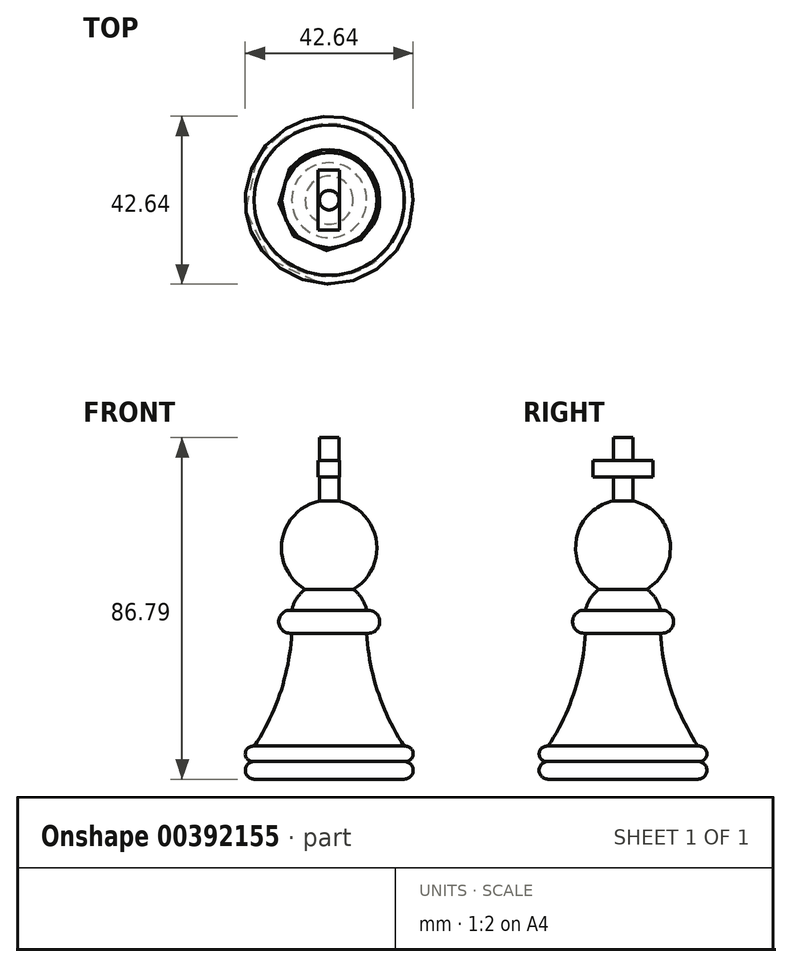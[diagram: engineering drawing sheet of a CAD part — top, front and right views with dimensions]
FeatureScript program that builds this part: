
annotation { "Feature Type Name" : "Feature", "Feature Type Description" : "" }
export const myFeature = defineFeature(function(context is Context, id is Id, definition is map)
    precondition{}
    {
        {
            var Q0;
            Q0=qCreatedBy(makeId("Front.planeOp"),FACE);
            var sketch = newSketch(context, id + "F0", { "sketchPlane" : qUnion([Q0])});
            skLineSegment(sketch, "E0", {"start": v(0, 33.3) * mm, "end": v(0, -42.9) * mm});
            skLineSegment(sketch, "E1", {"start": v(0, -42.9) * mm, "end": v(-19.05, -42.9) * mm});
            skArc(sketch, "E2", {"start": v(-19.05, -38.4) * mm, "mid": v(-21.3, -40.65) * mm, "end": v(-19.05, -42.9) * mm});
            skArc(sketch, "E3", {"start": v(-19.05, -34.52) * mm, "mid": v(-21.32, -36.46) * mm, "end": v(-19.05, -38.4) * mm});
            skArc(sketch, "E4", {"start": v(-19.05, -34.52) * mm, "mid": v(-12.38, -20.8) * mm, "end": v(-9.52, -5.8) * mm});
            skPoint(sketch, "E4.endSnap0", {"position": v(-9.52, -42.9) * mm});
            skArc(sketch, "E5", {"start": v(-9.53, 0) * mm, "mid": v(-12.84, -2.9) * mm, "end": v(-9.52, -5.8) * mm});
            skArc(sketch, "E6", {"start": v(-6.1, 5.34) * mm, "mid": v(-8.3, 2.98) * mm, "end": v(-9.53, 0) * mm});
            skArc(sketch, "E7", {"start": v(-2.48, 27.8) * mm, "mid": v(-11.97, 17.8) * mm, "end": v(-6.1, 5.34) * mm});
            skLineSegment(sketch, "E8", {"start": v(-2.48, 27.8) * mm, "end": v(-2.48, 43.88) * mm});
            skLineSegment(sketch, "E9", {"start": v(-2.48, 43.88) * mm, "end": v(0, 43.88) * mm});
            skLineSegment(sketch, "E10", {"start": v(0, 43.88) * mm, "end": v(0, 33.3) * mm});
            skPoint(sketch, "E11.orphan", {"position": v(0, 28.07) * mm});
            skSolve(sketch);
        }
        {
            var Q0;
            Q0=qSketchRegion(id+"F0",true);
            var Q1;
            Q1=sQuery(id+"F0.wireOp",EDGE,"E0");
            revolve(context, id + "F1", {"entities" : qUnion([Q0]), "axis" : qUnion([Q1]), "revolveType" : RevolveType.FULL});
        }
        {
            var Q0;
            Q0=qCreatedBy(makeId("Front.planeOp"),FACE);
            var sketch = newSketch(context, id + "F2", { "sketchPlane" : qUnion([Q0])});
            skLineSegment(sketch, "E12.bottom", {"start": v(-2.9, 38.07) * mm, "end": v(2.58, 38.07) * mm});
            skLineSegment(sketch, "E12.top", {"start": v(-2.9, 33.88) * mm, "end": v(2.58, 33.88) * mm});
            skLineSegment(sketch, "E12.left", {"start": v(-2.9, 38.07) * mm, "end": v(-2.9, 33.88) * mm});
            skLineSegment(sketch, "E12.right", {"start": v(2.58, 38.07) * mm, "end": v(2.58, 33.88) * mm});
            skSolve(sketch);
        }
        {
            var Q0;
            Q0=qSketchRegion(id+"F2",true);
            extrude(context, id + "F3", {"entities" : qUnion([Q0]), "operationType" : NewBodyOperationType.ADD, "depth" : 7.62 * mm});
        }
        {
            var Q0;
            Q0=qSketchRegion(id+"F2",true);
            extrude(context, id + "F4", {"entities" : qUnion([Q0]), "operationType" : NewBodyOperationType.ADD, "oppositeDirection" : true, "depth" : 7.62 * mm});
        }
    });
